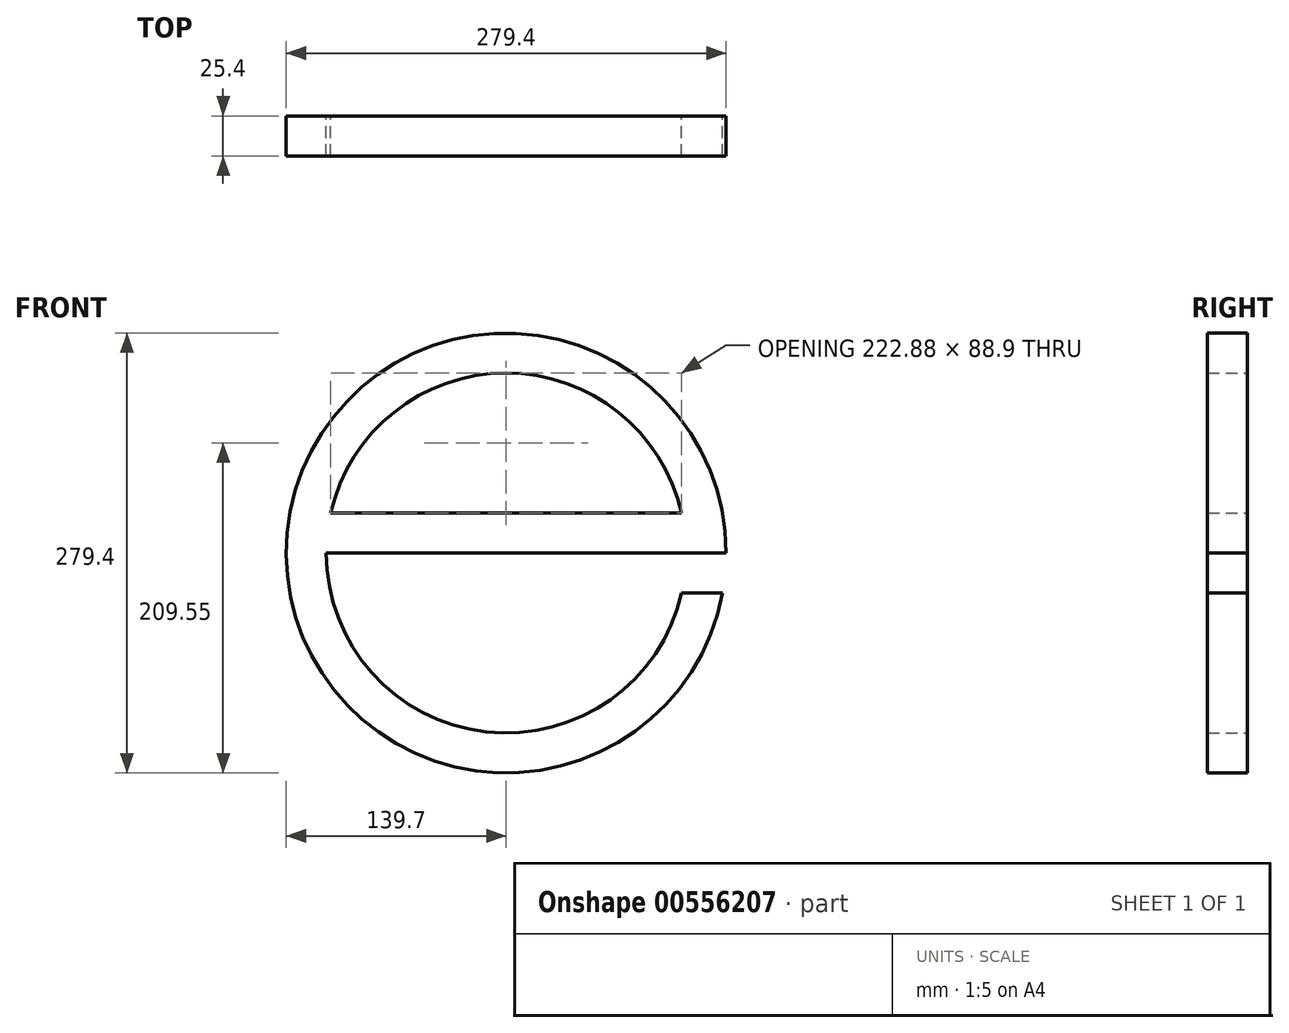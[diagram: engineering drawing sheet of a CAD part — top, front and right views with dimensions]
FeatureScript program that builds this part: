
annotation { "Feature Type Name" : "Feature", "Feature Type Description" : "" }
export const myFeature = defineFeature(function(context is Context, id is Id, definition is map)
    precondition{}
    {
        {
            var Q0;
            Q0=qCreatedBy(makeId("Front.planeOp"),FACE);
            var sketch = newSketch(context, id + "F0", { "sketchPlane" : qUnion([Q0])});
            skArc(sketch, "E0", {"start": v(139.7, 0) * mm, "mid": v(-139.12, 12.75) * mm, "end": v(137.37, -25.4) * mm});
            skArc(sketch, "E1", {"start": v(-114.3, 0) * mm, "mid": v(-12.78, -113.58) * mm, "end": v(111.44, -25.4) * mm});
            skLineSegment(sketch, "E2", {"start": v(139.7, 0) * mm, "end": v(-114.3, 0) * mm});
            skArc(sketch, "E3.trimOffspring", {"start": v(111.44, 25.4) * mm, "mid": v(0, 114.3) * mm, "end": v(-111.44, 25.4) * mm});
            skLineSegment(sketch, "E4.trimOffspring", {"start": v(111.44, 25.4) * mm, "end": v(-111.44, 25.4) * mm});
            skLineSegment(sketch, "E5", {"start": v(137.37, -25.4) * mm, "end": v(111.44, -25.4) * mm});
            skSolve(sketch);
        }
        {
            var Q0;
            Q0 = qSketchRegion(id + "F0", true);
            extrude(context, id + "F1", {"entities" : qUnion([Q0]), "depth" : 25.4 * mm, "offsetDistance" : 25.4 * mm});
        }
    });
